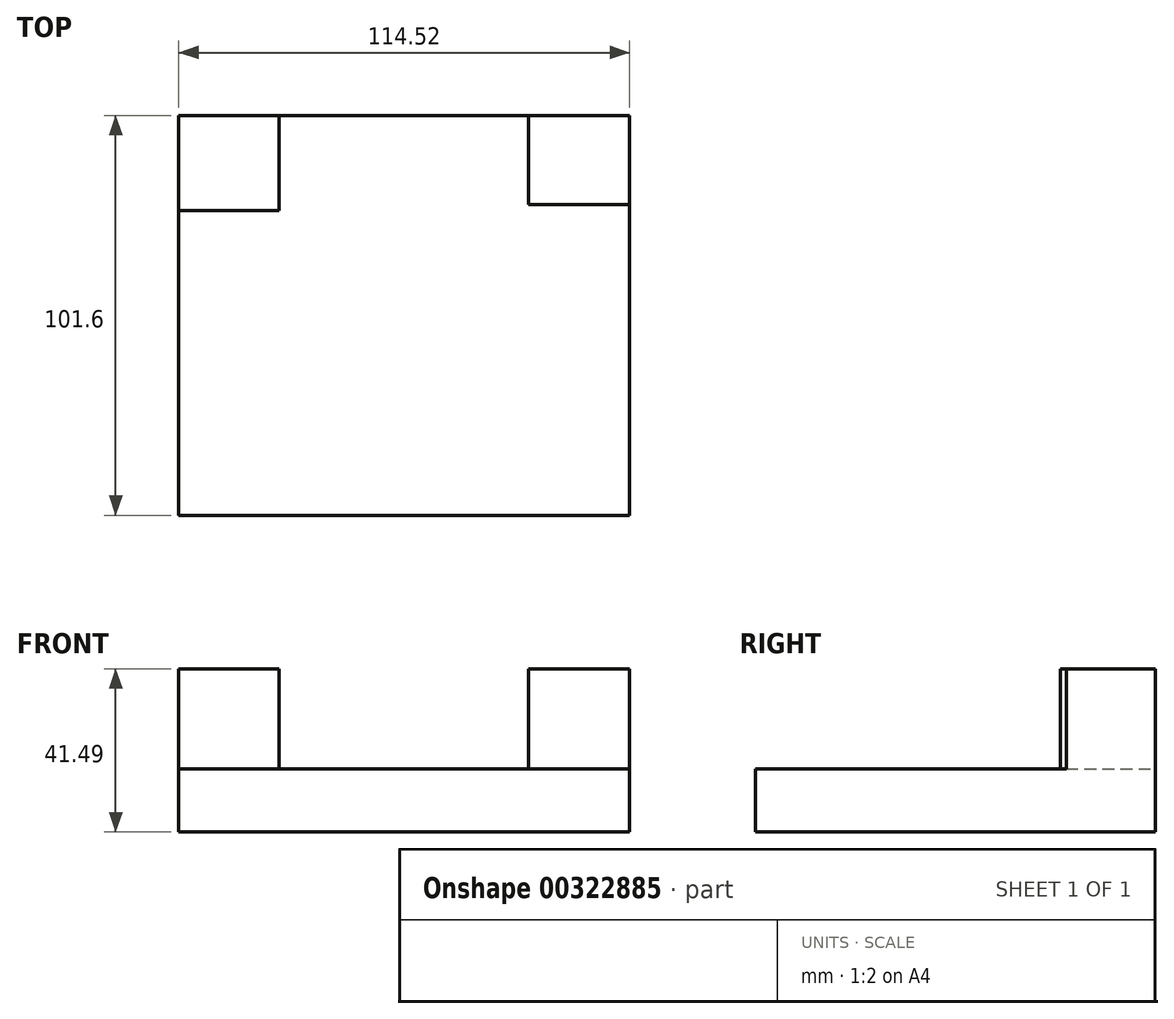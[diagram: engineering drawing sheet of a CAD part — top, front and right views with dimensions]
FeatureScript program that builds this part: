
annotation { "Feature Type Name" : "Feature", "Feature Type Description" : "" }
export const myFeature = defineFeature(function(context is Context, id is Id, definition is map)
    precondition{}
    {
        {
            var Q0;
            Q0=qCreatedBy(makeId("Front.planeOp"),FACE);
            var sketch = newSketch(context, id + "F0", { "sketchPlane" : qUnion([Q0])});
            skLineSegment(sketch, "E0", {"start": v(-56.33, -47.51) * mm, "end": v(58.19, -47.51) * mm});
            skLineSegment(sketch, "E1", {"start": v(58.19, -47.51) * mm, "end": v(58.19, -31.42) * mm});
            skLineSegment(sketch, "E2", {"start": v(58.19, -31.42) * mm, "end": v(-56.33, -31.42) * mm});
            skLineSegment(sketch, "E3", {"start": v(-56.33, -31.42) * mm, "end": v(-56.33, -47.51) * mm});
            skSolve(sketch);
        }
        {
            var Q0;
            Q0=makeQuery(id+"F0.imprint","IMPRINT",FACE,{"disambiguationData":[TD([[makeQuery(id+"F0.imprint","IMPRINT",EDGE,{"derivedFrom":sQuery(id+"F0.wireOp",EDGE,"E0")}),1.0]])]});
            extrude(context, id + "F1", {"entities" : qUnion([Q0]), "depth" : 101.6 * mm});
        }
        {
            var Q0;
            Q0=makeQuery(id+"F1.opExtrude","SWEPT_FACE",FACE,{"disambiguationData":[OSD([sQuery(id+"F0.wireOp",EDGE,"E2")])]});
            var sketch = newSketch(context, id + "F2", { "sketchPlane" : qUnion([Q0])});
            skLineSegment(sketch, "E4.bottom", {"start": v(58.19, -22.66) * mm, "end": v(32.54, -22.66) * mm});
            skLineSegment(sketch, "E4.top", {"start": v(58.19, 0) * mm, "end": v(32.54, 0) * mm});
            skLineSegment(sketch, "E4.left", {"start": v(58.19, -22.66) * mm, "end": v(58.19, 0) * mm});
            skLineSegment(sketch, "E4.right", {"start": v(32.54, -22.66) * mm, "end": v(32.54, 0) * mm});
            skSolve(sketch);
        }
        {
            var Q0;
            Q0=makeQuery(id+"F2.imprint","IMPRINT",FACE,{"disambiguationData":[TD([[makeQuery(id+"F2.imprint","IMPRINT",EDGE,{"derivedFrom":sQuery(id+"F2.wireOp",EDGE,"E4.bottom")}),-1.0]])]});
            extrude(context, id + "F3", {"entities" : qUnion([Q0]), "operationType" : NewBodyOperationType.ADD, "depth" : 25.4 * mm});
        }
        {
            var Q0;
            Q0=makeQuery(id+"F1.opExtrude","SWEPT_FACE",FACE,{"disambiguationData":[OSD([sQuery(id+"F0.wireOp",EDGE,"E2")])]});
            var sketch = newSketch(context, id + "F4", { "sketchPlane" : qUnion([Q0])});
            skLineSegment(sketch, "E5.bottom", {"start": v(-56.33, -15.3) * mm, "end": v(-30.89, -15.3) * mm});
            skLineSegment(sketch, "E5.top", {"start": v(-56.33, 0) * mm, "end": v(-30.89, 0) * mm});
            skLineSegment(sketch, "E5.left", {"start": v(-56.33, -15.3) * mm, "end": v(-56.33, 0) * mm});
            skLineSegment(sketch, "E5.right", {"start": v(-30.89, -15.3) * mm, "end": v(-30.89, 0) * mm});
            skSolve(sketch);
        }
        {
            var Q0;
            Q0=makeQuery(id+"F4.imprint","IMPRINT",FACE,{"disambiguationData":[TD([[makeQuery(id+"F4.imprint","IMPRINT",EDGE,{"derivedFrom":sQuery(id+"F4.wireOp",EDGE,"E5.bottom")}),1.0]])]});
            extrude(context, id + "F5", {"entities" : qUnion([Q0]), "operationType" : NewBodyOperationType.ADD, "depth" : 25.4 * mm});
        }
        {
            var Q0;
            Q0=makeQuery(id+"F5.opExtrude","SWEPT_FACE",FACE,{"disambiguationData":[OSD([sQuery(id+"F4.wireOp",EDGE,"E5.bottom")])]});
            extrude(context, id + "F6", {"entities" : qUnion([Q0]), "operationType" : NewBodyOperationType.ADD, "depth" : 8.9 * mm});
        }
    });
